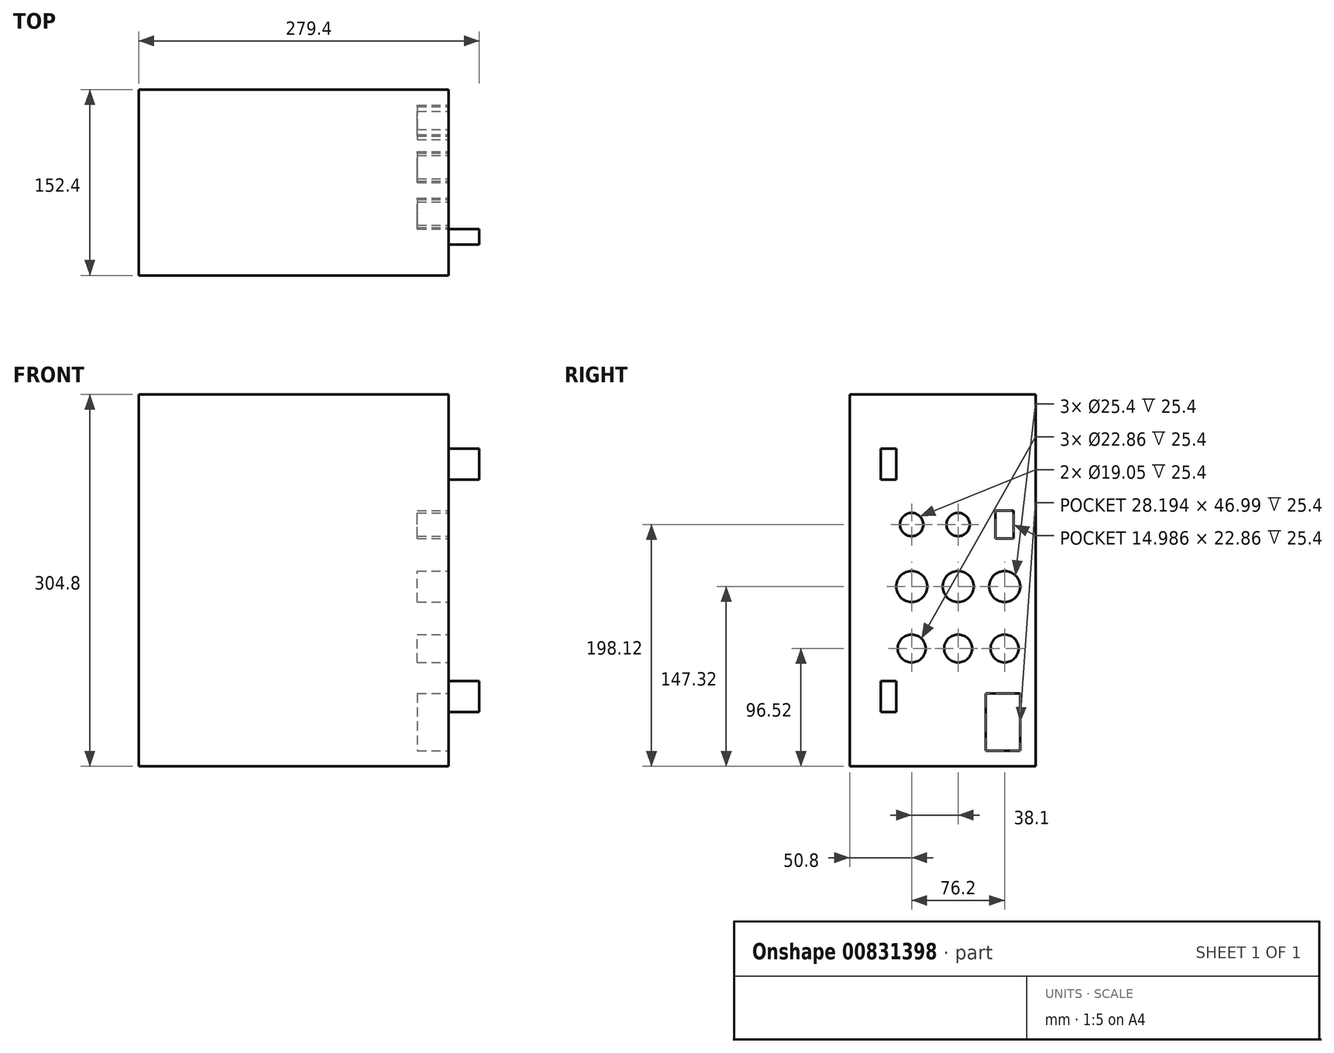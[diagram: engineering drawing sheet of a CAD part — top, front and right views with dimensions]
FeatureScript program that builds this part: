
annotation { "Feature Type Name" : "Feature", "Feature Type Description" : "" }
export const myFeature = defineFeature(function(context is Context, id is Id, definition is map)
    precondition{}
    {
        {
            var Q0;
            Q0=qCreatedBy(makeId("Front.planeOp"),FACE);
            var sketch = newSketch(context, id + "F0", { "sketchPlane" : qUnion([Q0])});
            skLineSegment(sketch, "E0.bottom", {"start": v(-127, 152.4) * mm, "end": v(127, 152.4) * mm});
            skLineSegment(sketch, "E0.top", {"start": v(-127, -152.4) * mm, "end": v(127, -152.4) * mm});
            skLineSegment(sketch, "E0.left", {"start": v(-127, 152.4) * mm, "end": v(-127, -152.4) * mm});
            skLineSegment(sketch, "E0.right", {"start": v(127, 152.4) * mm, "end": v(127, -152.4) * mm});
            skPoint(sketch, "E0.middle", {"position": v(0, 0) * mm});
            skSolve(sketch);
        }
        {
            var Q0;
            Q0 = qSketchRegion(id + "F0", true);
            extrude(context, id + "F1", {"entities" : qUnion([Q0]), "depth" : 152.4 * mm, "offsetDistance" : 25.4 * mm});
        }
        {
            var Q0;
            Q0=makeQuery(id+"F1.opExtrude","SWEPT_FACE",FACE,{"disambiguationData":[OSD([sQuery(id+"F0.wireOp",EDGE,"E0.right")])]});
            var sketch = newSketch(context, id + "F2", { "sketchPlane" : qUnion([Q0])});
            skLineSegment(sketch, "E1.bottom", {"start": v(-114.3, 107.95) * mm, "end": v(-127, 107.95) * mm});
            skLineSegment(sketch, "E1.top", {"start": v(-114.3, 82.55) * mm, "end": v(-127, 82.55) * mm});
            skLineSegment(sketch, "E1.left", {"start": v(-114.3, 107.95) * mm, "end": v(-114.3, 82.55) * mm});
            skLineSegment(sketch, "E1.right", {"start": v(-127, 107.95) * mm, "end": v(-127, 82.55) * mm});
            skLineSegment(sketch, "E2.bottom", {"start": v(-114.3, -107.95) * mm, "end": v(-127, -107.95) * mm});
            skLineSegment(sketch, "E2.top", {"start": v(-114.3, -82.55) * mm, "end": v(-127, -82.55) * mm});
            skLineSegment(sketch, "E2.left", {"start": v(-114.3, -107.95) * mm, "end": v(-114.3, -82.55) * mm});
            skLineSegment(sketch, "E2.right", {"start": v(-127, -107.95) * mm, "end": v(-127, -82.55) * mm});
            skSolve(sketch);
        }
        {
            var Q0;
            Q0 = qSketchRegion(id + "F2", true);
            extrude(context, id + "F3", {"entities" : qUnion([Q0]), "operationType" : NewBodyOperationType.ADD, "depth" : 25.4 * mm, "offsetDistance" : 25.4 * mm});
        }
        {
            var Q0;
            Q0=makeQuery(id+"F1.opExtrude","SWEPT_FACE",FACE,{"disambiguationData":[OSD([sQuery(id+"F0.wireOp",EDGE,"E0.right")])]});
            var sketch = newSketch(context, id + "F4", { "sketchPlane" : qUnion([Q0])});
            skCircle(sketch, "E3", {"center": v(-101.6, -5.08) * mm, "radius": 12.7 * mm});
            skCircle(sketch, "E4", {"center": v(-63.5, -5.08) * mm, "radius": 12.7 * mm});
            skCircle(sketch, "E5", {"center": v(-25.4, -5.08) * mm, "radius": 12.7 * mm});
            skCircle(sketch, "E6", {"center": v(-101.6, -55.88) * mm, "radius": 11.43 * mm});
            skCircle(sketch, "E7", {"center": v(-63.5, -55.88) * mm, "radius": 11.43 * mm});
            skCircle(sketch, "E8", {"center": v(-25.4, -55.88) * mm, "radius": 11.43 * mm});
            skLineSegment(sketch, "E9", {"start": v(-101.6, -5.08) * mm, "end": v(-63.5, -5.08) * mm, "construction": true});
            skLineSegment(sketch, "E10", {"start": v(-25.4, -5.08) * mm, "end": v(-63.5, -5.08) * mm, "construction": true});
            skLineSegment(sketch, "E11.1", {"start": v(0, 152.4) * mm, "end": v(0, -152.4) * mm});
            skLineSegment(sketch, "E12", {"start": v(-63.5, -55.88) * mm, "end": v(-63.5, -5.08) * mm, "construction": true});
            skLineSegment(sketch, "E13", {"start": v(-101.6, -5.08) * mm, "end": v(-101.6, -55.88) * mm, "construction": true});
            skLineSegment(sketch, "E14", {"start": v(-25.4, -5.08) * mm, "end": v(-25.4, -55.88) * mm, "construction": true});
            skLineSegment(sketch, "E15.bottom", {"start": v(-12.7, -92.71) * mm, "end": v(-40.9, -92.71) * mm});
            skLineSegment(sketch, "E15.top", {"start": v(-12.7, -139.7) * mm, "end": v(-40.9, -139.7) * mm});
            skLineSegment(sketch, "E15.left", {"start": v(-12.7, -92.71) * mm, "end": v(-12.7, -139.7) * mm});
            skLineSegment(sketch, "E15.right", {"start": v(-40.9, -92.71) * mm, "end": v(-40.9, -139.7) * mm});
            skLineSegment(sketch, "E16.bottom", {"start": v(-32.9, 34.29) * mm, "end": v(-17.9, 34.29) * mm});
            skLineSegment(sketch, "E16.top", {"start": v(-32.9, 57.15) * mm, "end": v(-17.9, 57.15) * mm});
            skLineSegment(sketch, "E16.left", {"start": v(-32.9, 34.29) * mm, "end": v(-32.9, 57.15) * mm});
            skLineSegment(sketch, "E16.right", {"start": v(-17.9, 34.29) * mm, "end": v(-17.9, 57.15) * mm});
            skPoint(sketch, "E16.middle", {"position": v(-25.4, 45.72) * mm});
            skCircle(sketch, "E17", {"center": v(-101.6, 45.72) * mm, "radius": 9.53 * mm});
            skLineSegment(sketch, "E18", {"start": v(-101.6, 45.72) * mm, "end": v(-101.6, -5.08) * mm, "construction": true});
            skLineSegment(sketch, "E19", {"start": v(-25.4, 45.72) * mm, "end": v(-101.6, 45.72) * mm, "construction": true});
            skLineSegment(sketch, "E20", {"start": v(-101.6, -55.88) * mm, "end": v(-63.5, -55.88) * mm, "construction": true});
            skLineSegment(sketch, "E21", {"start": v(-63.5, -55.88) * mm, "end": v(-25.4, -55.88) * mm, "construction": true});
            skLineSegment(sketch, "E22", {"start": v(-25.4, 45.72) * mm, "end": v(-25.4, -5.08) * mm, "construction": true});
            skCircle(sketch, "E23", {"center": v(-63.5, 45.72) * mm, "radius": 9.53 * mm});
            skLineSegment(sketch, "E24", {"start": v(-63.5, -5.08) * mm, "end": v(-63.5, 45.72) * mm, "construction": true});
            skSolve(sketch);
        }
        {
            var Q0;
            Q0 = qSketchRegion(id + "F4", true);
            extrude(context, id + "F5", {"entities" : qUnion([Q0]), "operationType" : NewBodyOperationType.REMOVE, "oppositeDirection" : true, "depth" : 25.4 * mm, "offsetDistance" : 25.4 * mm});
        }
    });
